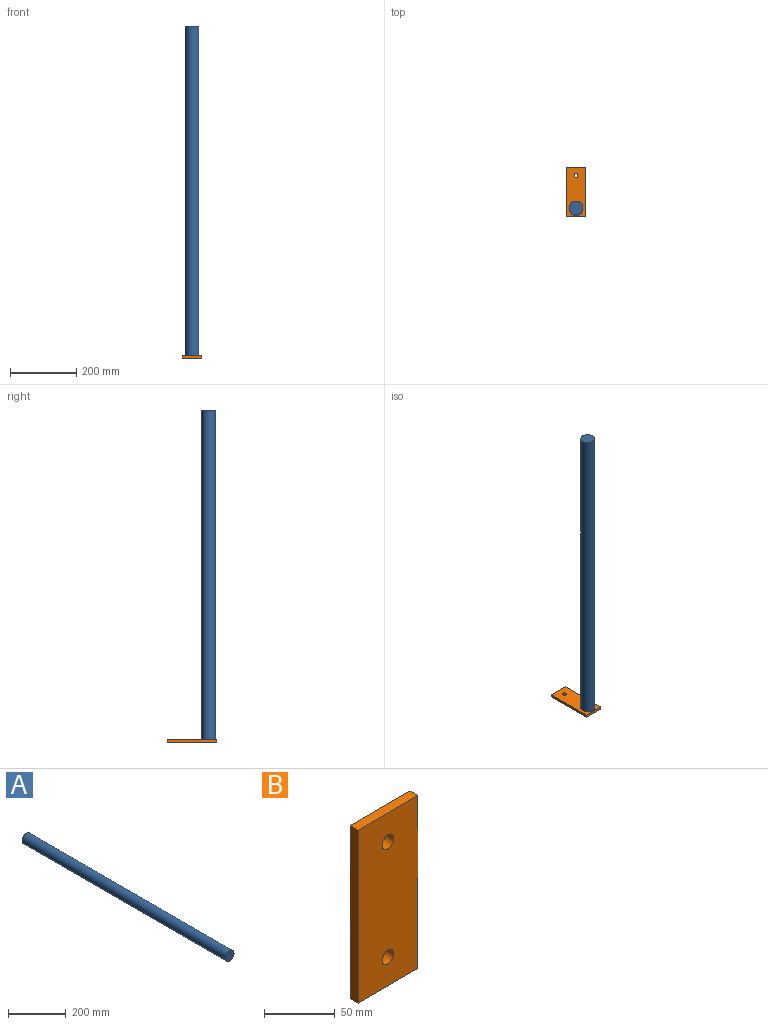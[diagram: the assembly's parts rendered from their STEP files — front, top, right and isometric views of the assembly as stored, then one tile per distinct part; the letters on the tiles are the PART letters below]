
ASSEMBLY  parts=2 mates=1
PART A: 3 faces, bbox 42x992x42 mm
  f0: cylinder r=21mm len=992mm, axis (0,1,0), area 130891.3mm2, adj f1,f2
  f1: plane 42x42mm, normal (0,-1,0), area 1385.4mm2, adj f0
  f2: plane 42x42mm, normal (0,1,0), area 1385.4mm2, adj f0
PART B: 8 faces, bbox 60x8x150 mm
  f0: plane 60x8mm, normal (0,0,-1), area 480mm2, adj f1,f5,f6,f7
  f1: plane 150x8mm, normal (1,0,0), area 1200mm2, adj f0,f2,f6,f7
  f2: plane 60x8mm, normal (0,0,1), area 480mm2, adj f1,f5,f6,f7
  f3: cylinder r=6mm len=12mm, axis (0,1,0), area 301.6mm2, adj f6,f7
  f4: cylinder r=6mm len=12mm, axis (0,1,0), area 301.6mm2, adj f6,f7
  f5: plane 150x8mm, normal (-1,0,0), area 1200mm2, adj f0,f2,f6,f7
  f6: plane 150x60mm, normal (0,-1,0), area 8773.8mm2, adj f0,f1,f2,f3,f4,f5
  f7: plane 150x60mm, normal (0,1,0), area 8773.8mm2, adj f0,f1,f2,f3,f4,f5
PLACE A rot(axis=(-1,0,0),90deg) t=(10.6,-91.83,39.41)mm
PLACE B rot(axis=(-1,0,0),90deg) t=(10.6,-41.83,35.41)mm
MATE fastened A.f0 <-> B.f4  axis (0,0,-1) through (10.6,-91.83,39.41)mm
